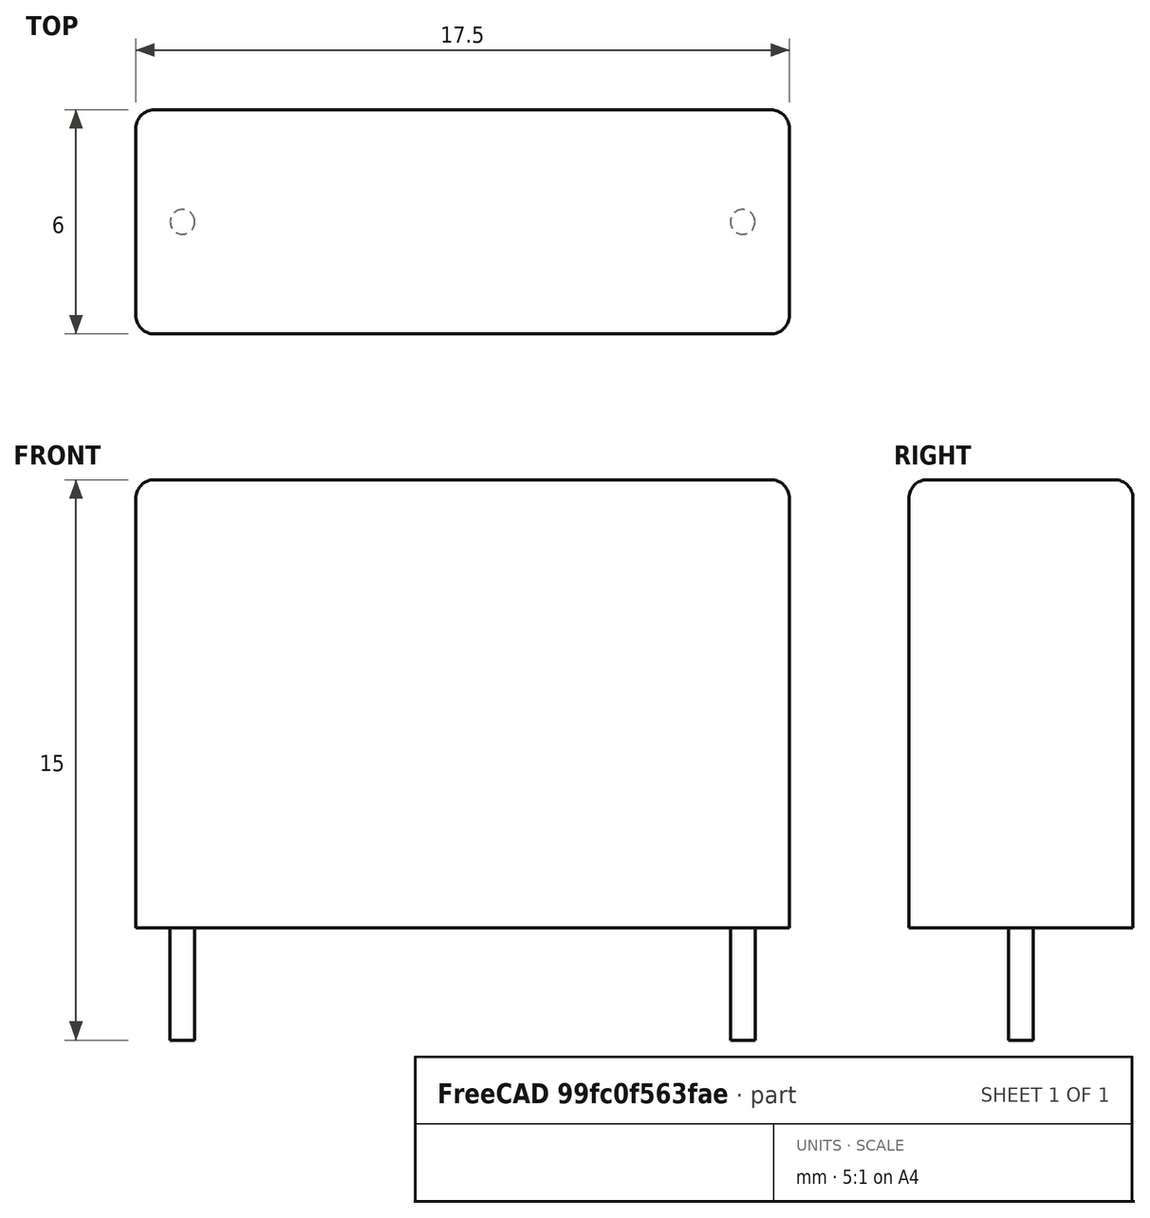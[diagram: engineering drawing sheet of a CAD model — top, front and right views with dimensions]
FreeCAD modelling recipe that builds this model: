
FCSTD DOCUMENT
Label: CAPARV1500W60L1750T600H1200
objects: Part::Cylinder×2, Part::Fuse×2, Part::Box×1, Part::Fillet×1
note: 6 computed .brp shape members not serialized (recipe doc carries the construction recipe); baked Part::Feature solids carry a one-line shape summary decoded from their .brp

FEATURE [Part::Cylinder] Cylinder  label="Pin1"
  Angle = 360
  Height = 3
  Placement = pos=(-7.5,0,-3) rot=(0,0,1;0rad)
  Radius = 0.33
FEATURE [Part::Cylinder] Cylinder001  label="Pin2"
  Angle = 360
  Height = 3
  Placement = pos=(7.5,0,-3) rot=(0,0,1;0rad)
  Radius = 0.33
FEATURE [Part::Box] Box  label="Grundkoerper"
  Height = 12
  Length = 17.5
  Placement = pos=(-8.75,-3,0) rot=(0,0,1;0rad)
  Width = 6
FEATURE [Part::Fillet] Fillet
  Base = -> Box
  Edges = 8 edges r=0.5: [Edge1,Edge2,Edge3,Edge5,Edge6,Edge7,Edge10,Edge12]
FEATURE [Part::Fuse] Fusion
  Base = -> Fillet
  Tool = -> Cylinder
FEATURE [Part::Fuse] Fusion001  label="CAPARV1500W60L1750T600H1200"
  Base = -> Fusion
  Tool = -> Cylinder001
